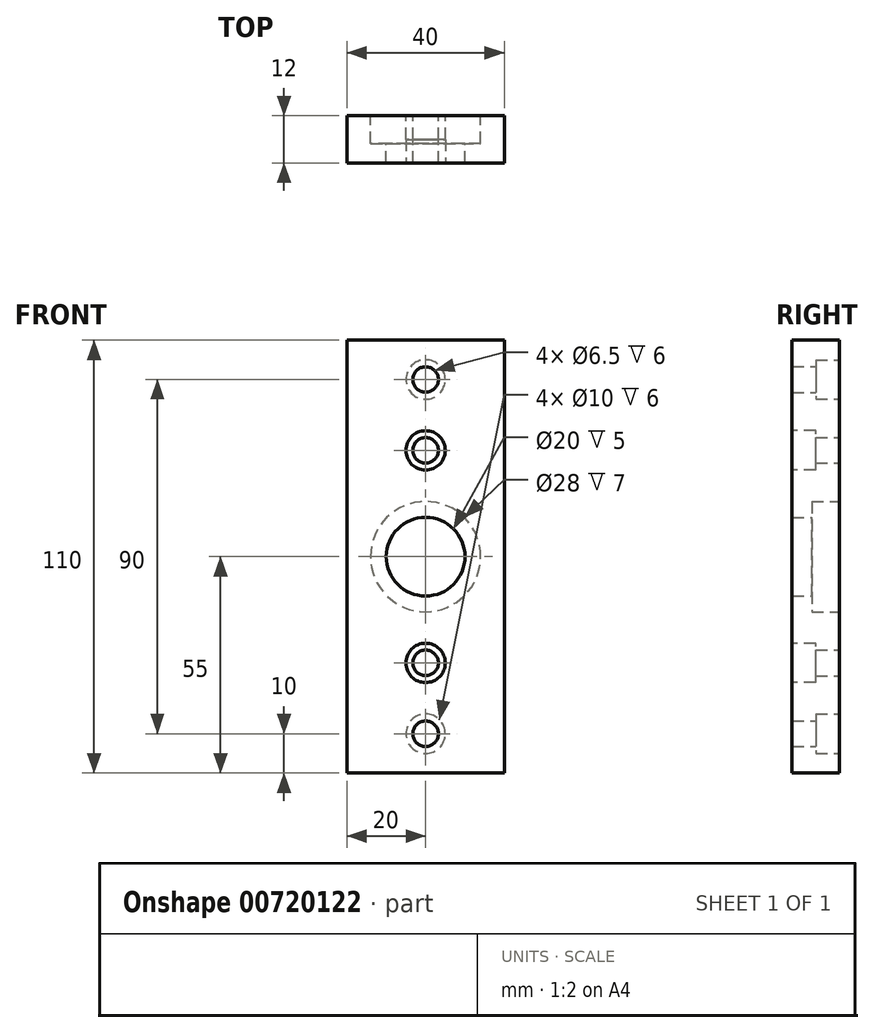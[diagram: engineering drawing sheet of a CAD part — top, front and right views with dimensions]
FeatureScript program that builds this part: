
annotation { "Feature Type Name" : "Feature", "Feature Type Description" : "" }
export const myFeature = defineFeature(function(context is Context, id is Id, definition is map)
    precondition{}
    {
        {
            var Q0;
            Q0=qCreatedBy(makeId("Front.planeOp"),FACE);
            var sketch = newSketch(context, id + "F0", { "sketchPlane" : qUnion([Q0])});
            skLineSegment(sketch, "E0.bottom", {"start": v(0, 0) * mm, "end": v(40, 0) * mm});
            skLineSegment(sketch, "E0.top", {"start": v(0, 110) * mm, "end": v(40, 110) * mm});
            skLineSegment(sketch, "E0.left", {"start": v(0, 0) * mm, "end": v(0, 110) * mm});
            skLineSegment(sketch, "E0.right", {"start": v(40, 0) * mm, "end": v(40, 110) * mm});
            skCircle(sketch, "E1", {"center": v(20, 55) * mm, "radius": 10 * mm});
            skPoint(sketch, "E1.centerSnap0", {"position": v(20, 110) * mm});
            skPoint(sketch, "E1.centerSnap1", {"position": v(0, 55) * mm});
            skCircle(sketch, "E2", {"center": v(20, 28) * mm, "radius": 3.25 * mm});
            skPoint(sketch, "E2.centerSnap0", {"position": v(20, 0) * mm});
            skCircle(sketch, "E3", {"center": v(20, 82) * mm, "radius": 3.25 * mm});
            skCircle(sketch, "E4", {"center": v(20, 100) * mm, "radius": 3.25 * mm});
            skCircle(sketch, "E5", {"center": v(20, 10) * mm, "radius": 3.25 * mm});
            skSolve(sketch);
        }
        {
            var Q0;
            Q0=makeQuery(id+"F0.imprint","IMPRINT",FACE,{"disambiguationData":[TD([[makeQuery(id+"F0.imprint","IMPRINT",EDGE,{"derivedFrom":sQuery(id+"F0.wireOp",EDGE,"E0.bottom")}),1.0]])]});
            extrude(context, id + "F1", {"entities" : qUnion([Q0]), "depth" : 12 * mm, "offsetDistance" : 25 * mm});
        }
        {
            var Q0;
            Q0=makeQuery(id+"F1.opExtrude","CAP_FACE",FACE,{"disambiguationData":[OSD([sQuery(id+"F0.wireOp",EDGE,"E0.bottom"),sQuery(id+"F0.wireOp",EDGE,"E0.top"),sQuery(id+"F0.wireOp",EDGE,"E0.left"),sQuery(id+"F0.wireOp",EDGE,"E0.right"),sQuery(id+"F0.wireOp",EDGE,"E1"),sQuery(id+"F0.wireOp",EDGE,"E2"),sQuery(id+"F0.wireOp",EDGE,"E3"),sQuery(id+"F0.wireOp",EDGE,"E4"),sQuery(id+"F0.wireOp",EDGE,"E5")])],"isStart":false});
            var sketch = newSketch(context, id + "F2", { "sketchPlane" : qUnion([Q0])});
            skCircle(sketch, "E6", {"center": v(20, 82) * mm, "radius": 5 * mm});
            skCircle(sketch, "E7", {"center": v(20, 28) * mm, "radius": 5 * mm});
            skSolve(sketch);
        }
        {
            var Q0;
            Q0 = qSketchRegion(id + "F2", true);
            extrude(context, id + "F3", {"entities" : qUnion([Q0]), "operationType" : NewBodyOperationType.REMOVE, "oppositeDirection" : true, "depth" : 6 * mm, "offsetDistance" : 25 * mm});
        }
        {
            var Q0;
            Q0=makeQuery(id+"F1.opExtrude","CAP_FACE",FACE,{"disambiguationData":[OSD([sQuery(id+"F0.wireOp",EDGE,"E0.bottom"),sQuery(id+"F0.wireOp",EDGE,"E0.top"),sQuery(id+"F0.wireOp",EDGE,"E0.left"),sQuery(id+"F0.wireOp",EDGE,"E0.right"),sQuery(id+"F0.wireOp",EDGE,"E1"),sQuery(id+"F0.wireOp",EDGE,"E2"),sQuery(id+"F0.wireOp",EDGE,"E3"),sQuery(id+"F0.wireOp",EDGE,"E4"),sQuery(id+"F0.wireOp",EDGE,"E5")])],"isStart":true});
            var sketch = newSketch(context, id + "F4", { "sketchPlane" : qUnion([Q0])});
            skCircle(sketch, "E8", {"center": v(-20, 100) * mm, "radius": 5 * mm});
            skCircle(sketch, "E9", {"center": v(-20, 10) * mm, "radius": 5 * mm});
            skSolve(sketch);
        }
        {
            var Q0;
            Q0 = qSketchRegion(id + "F4", true);
            extrude(context, id + "F5", {"entities" : qUnion([Q0]), "operationType" : NewBodyOperationType.REMOVE, "oppositeDirection" : true, "depth" : 6 * mm, "offsetDistance" : 25 * mm});
        }
        {
            var Q0;
            Q0=makeQuery(id+"F1.opExtrude","CAP_FACE",FACE,{"disambiguationData":[OSD([sQuery(id+"F0.wireOp",EDGE,"E0.bottom"),sQuery(id+"F0.wireOp",EDGE,"E0.top"),sQuery(id+"F0.wireOp",EDGE,"E0.left"),sQuery(id+"F0.wireOp",EDGE,"E0.right"),sQuery(id+"F0.wireOp",EDGE,"E1"),sQuery(id+"F0.wireOp",EDGE,"E2"),sQuery(id+"F0.wireOp",EDGE,"E3"),sQuery(id+"F0.wireOp",EDGE,"E4"),sQuery(id+"F0.wireOp",EDGE,"E5")])],"isStart":true});
            var sketch = newSketch(context, id + "F6", { "sketchPlane" : qUnion([Q0])});
            skCircle(sketch, "E10", {"center": v(-20, 55) * mm, "radius": 14 * mm});
            skSolve(sketch);
        }
        {
            var Q0;
            Q0=makeQuery(id+"F6.imprint","IMPRINT",FACE,{"disambiguationData":[TD([[makeQuery(id+"F6.imprint","IMPRINT",EDGE,{"derivedFrom":sQuery(id+"F6.wireOp",EDGE,"E10")}),1.0]])]});
            extrude(context, id + "F7", {"entities" : qUnion([Q0]), "operationType" : NewBodyOperationType.REMOVE, "oppositeDirection" : true, "depth" : 7 * mm, "offsetDistance" : 25 * mm});
        }
    });
